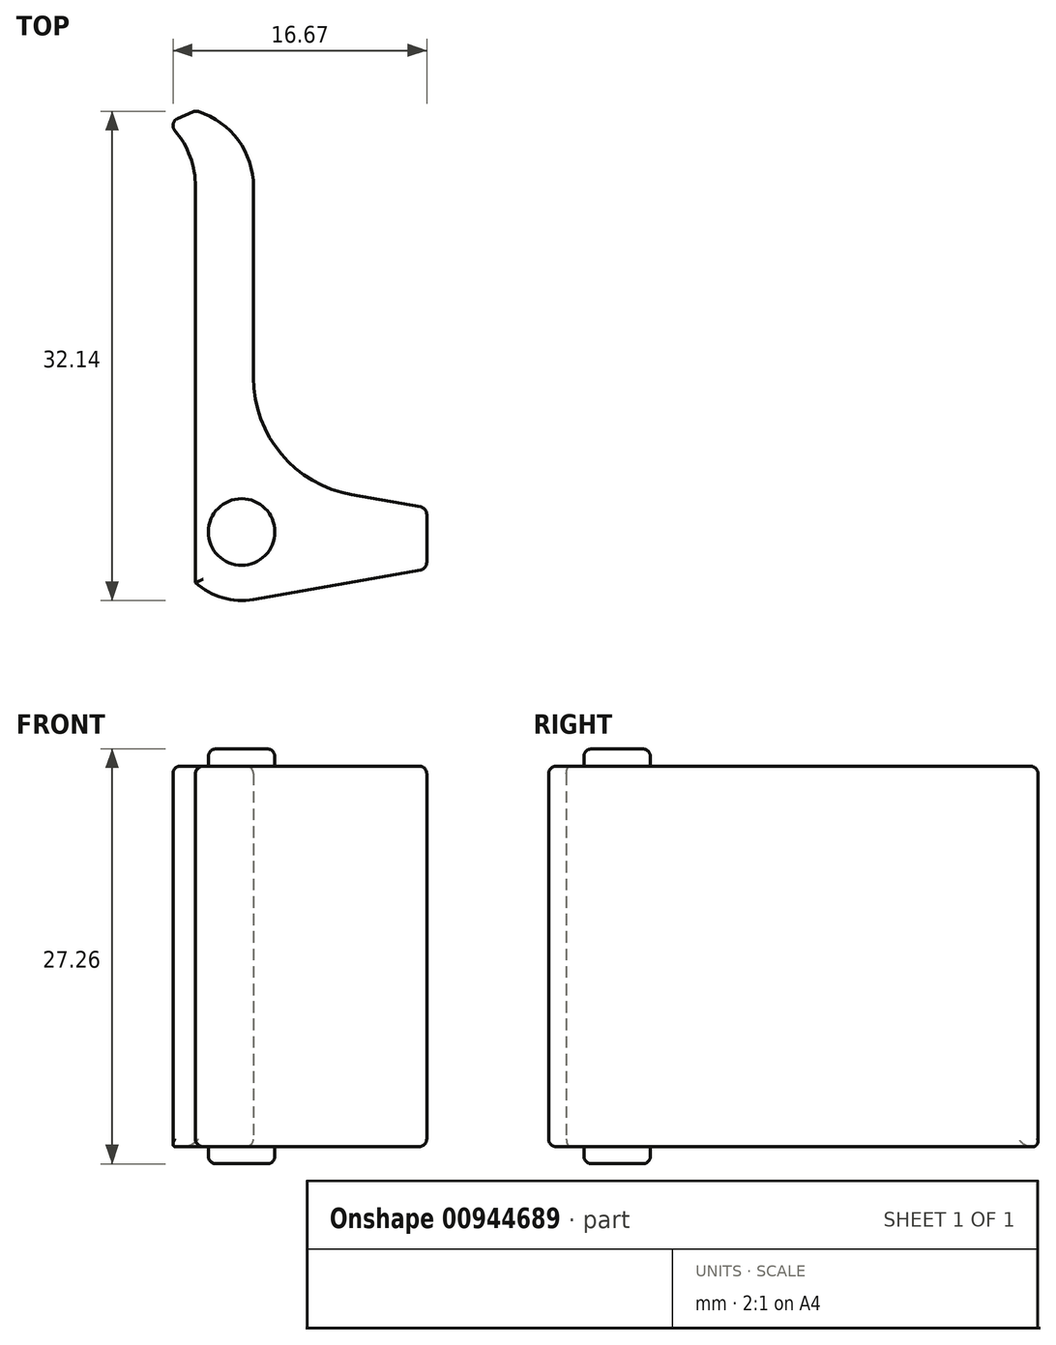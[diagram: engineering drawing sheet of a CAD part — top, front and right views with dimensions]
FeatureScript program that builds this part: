
annotation { "Feature Type Name" : "Feature", "Feature Type Description" : "" }
export const myFeature = defineFeature(function(context is Context, id is Id, definition is map)
    precondition{}
    {
        {
            var Q0;
            Q0=qCreatedBy(makeId("Top.planeOp"),FACE);
            var sketch = newSketch(context, id + "F0", { "sketchPlane" : qUnion([Q0])});
            skLineSegment(sketch, "E0", {"start": v(0, 0) * mm, "end": v(0, 26) * mm});
            skLineSegment(sketch, "E1", {"start": v(3.8, 26) * mm, "end": v(3.8, 13.46) * mm});
            skArc(sketch, "E2", {"start": v(3.8, 13.46) * mm, "mid": v(5.64, 8.44) * mm, "end": v(10.26, 5.77) * mm});
            skLineSegment(sketch, "E3", {"start": v(10.26, 5.77) * mm, "end": v(15.19, 4.9) * mm});
            skLineSegment(sketch, "E4", {"start": v(15.19, 4.9) * mm, "end": v(15.19, 0.9) * mm});
            skLineSegment(sketch, "E5", {"start": v(15.19, 0.9) * mm, "end": v(3.8, -1.1) * mm});
            skArc(sketch, "E6", {"start": v(0, 0) * mm, "mid": v(1.78, -1) * mm, "end": v(3.8, -1.1) * mm});
            skLineSegment(sketch, "E7", {"start": v(0, 26) * mm, "end": v(52.42, 26) * mm, "construction": true});
            skCircle(sketch, "E8", {"center": v(3.03, 3.33) * mm, "radius": 2.19 * mm});
            skPoint(sketch, "E9", {"position": v(15.19, 2.9) * mm});
            skPoint(sketch, "E10", {"position": v(1.14, 31.66) * mm});
            skLineSegment(sketch, "E11", {"start": v(1.14, 31.66) * mm, "end": v(15.19, 2.9) * mm, "construction": true});
            skLineSegment(sketch, "E12", {"start": v(3.03, 3.33) * mm, "end": v(3.03, -1.17) * mm, "construction": true});
            skArc(sketch, "E13", {"start": v(3.8, 26) * mm, "mid": v(2.75, 29.14) * mm, "end": v(0, 31) * mm});
            skLineSegment(sketch, "E14", {"start": v(1.14, 31.66) * mm, "end": v(-9.06, 26.67) * mm, "construction": true});
            skLineSegment(sketch, "E15", {"start": v(0, 31) * mm, "end": v(-1.83, 30.2) * mm});
            skArc(sketch, "E16", {"start": v(0, 26) * mm, "mid": v(-0.48, 28.3) * mm, "end": v(-1.83, 30.2) * mm});
            skSolve(sketch);
        }
        {
            var Q0;
            Q0=makeQuery(id+"F2.opExtrude","CAP_FACE",FACE,{"disambiguationData":[OSD([sQuery(id+"F0.wireOp",EDGE,"E0"),sQuery(id+"F0.wireOp",EDGE,"E1"),sQuery(id+"F0.wireOp",EDGE,"E2"),sQuery(id+"F0.wireOp",EDGE,"E3"),sQuery(id+"F0.wireOp",EDGE,"E4"),sQuery(id+"F0.wireOp",EDGE,"E5"),sQuery(id+"F0.wireOp",EDGE,"E6"),sQuery(id+"F0.wireOp",EDGE,"E13"),sQuery(id+"F0.wireOp",EDGE,"E15"),sQuery(id+"F0.wireOp",EDGE,"E16")])],"isStart":false});
            var Q1;
            Q1=makeQuery(id+"F0.imprint","IMPRINT",FACE,{"disambiguationData":[TD([[makeQuery(id+"F0.imprint","IMPRINT",EDGE,{"derivedFrom":sQuery(id+"F0.wireOp",EDGE,"E8")}),1.0]])]});
            extrude(context, id + "F1", {"entities" : qUnion([Q0, Q1]), "endBound" : BoundingType.SYMMETRIC, "depth" : 27.25 * mm, "offsetDistance" : 25 * mm});
        }
        {
            var Q0;
            Q0 = qSketchRegion(id + "F0", true);
            extrude(context, id + "F2", {"entities" : qUnion([Q0]), "operationType" : NewBodyOperationType.ADD, "endBound" : BoundingType.SYMMETRIC, "depth" : 25 * mm, "offsetDistance" : 25 * mm});
        }
        {
            var Q0;
            Q0=makeQuery(id+"F2.opExtrude","CAP_EDGE",EDGE,{"disambiguationData":[OSD([sQuery(id+"F0.wireOp",EDGE,"E6")])],"isStart":false});
            var Q1;
            Q1=makeQuery(id+"F2.opExtrude","CAP_EDGE",EDGE,{"disambiguationData":[OSD([sQuery(id+"F0.wireOp",EDGE,"E5")])],"isStart":false});
            var Q2;
            Q2=makeQuery(id+"F2.opExtrude","CAP_EDGE",EDGE,{"disambiguationData":[OSD([sQuery(id+"F0.wireOp",EDGE,"E0")])],"isStart":false});
            var Q3;
            Q3=makeQuery(id+"F2.opExtrude","CAP_EDGE",EDGE,{"disambiguationData":[OSD([sQuery(id+"F0.wireOp",EDGE,"E16")])],"isStart":false});
            var Q4;
            Q4=makeQuery(id+"F2.opExtrude","SWEPT_EDGE",EDGE,{"disambiguationData":[OSD([sQuery(id+"F0.wireOp",EDGE,"E15"),sQuery(id+"F0.wireOp",EDGE,"E16")])]});
            var Q5;
            Q5=makeQuery(id+"F2.opExtrude","SWEPT_EDGE",EDGE,{"disambiguationData":[OSD([sQuery(id+"F0.wireOp",EDGE,"E13"),sQuery(id+"F0.wireOp",EDGE,"E15")])]});
            var Q6;
            Q6=makeQuery(id+"F2.opExtrude","CAP_EDGE",EDGE,{"disambiguationData":[OSD([sQuery(id+"F0.wireOp",EDGE,"E0")])],"isStart":true});
            var Q7;
            Q7=makeQuery(id+"F2.opExtrude","CAP_EDGE",EDGE,{"disambiguationData":[OSD([sQuery(id+"F0.wireOp",EDGE,"E16")])],"isStart":true});
            var Q8;
            Q8=makeQuery(id+"F2.opExtrude","CAP_EDGE",EDGE,{"disambiguationData":[OSD([sQuery(id+"F0.wireOp",EDGE,"E13")])],"isStart":true});
            var Q9;
            Q9=makeQuery(id+"F2.opExtrude","CAP_EDGE",EDGE,{"disambiguationData":[OSD([sQuery(id+"F0.wireOp",EDGE,"E1")])],"isStart":true});
            var Q10;
            Q10=makeQuery(id+"F2.opExtrude","CAP_EDGE",EDGE,{"disambiguationData":[OSD([sQuery(id+"F0.wireOp",EDGE,"E2")])],"isStart":true});
            var Q11;
            Q11=makeQuery(id+"F2.opExtrude","CAP_EDGE",EDGE,{"disambiguationData":[OSD([sQuery(id+"F0.wireOp",EDGE,"E3")])],"isStart":true});
            var Q12;
            Q12=makeQuery(id+"F2.opExtrude","CAP_EDGE",EDGE,{"disambiguationData":[OSD([sQuery(id+"F0.wireOp",EDGE,"E4")])],"isStart":true});
            var Q13;
            Q13=makeQuery(id+"F2.opExtrude","CAP_EDGE",EDGE,{"disambiguationData":[OSD([sQuery(id+"F0.wireOp",EDGE,"E5")])],"isStart":true});
            var Q14;
            Q14=makeQuery(id+"F2.opExtrude","CAP_EDGE",EDGE,{"disambiguationData":[OSD([sQuery(id+"F0.wireOp",EDGE,"E6")])],"isStart":true});
            var Q15;
            Q15=makeQuery(id+"F2.opExtrude","SWEPT_EDGE",EDGE,{"disambiguationData":[OSD([sQuery(id+"F0.wireOp",EDGE,"E4"),sQuery(id+"F0.wireOp",EDGE,"E5")])]});
            var Q16;
            Q16=makeQuery(id+"F2.opExtrude","SWEPT_EDGE",EDGE,{"disambiguationData":[OSD([sQuery(id+"F0.wireOp",EDGE,"E3"),sQuery(id+"F0.wireOp",EDGE,"E4")])]});
            var Q17;
            Q17=makeQuery(id+"F2.opExtrude","CAP_EDGE",EDGE,{"disambiguationData":[OSD([sQuery(id+"F0.wireOp",EDGE,"E4")])],"isStart":false});
            var Q18;
            Q18=makeQuery(id+"F2.opExtrude","CAP_EDGE",EDGE,{"disambiguationData":[OSD([sQuery(id+"F0.wireOp",EDGE,"E3")])],"isStart":false});
            var Q19;
            Q19=makeQuery(id+"F2.opExtrude","CAP_EDGE",EDGE,{"disambiguationData":[OSD([sQuery(id+"F0.wireOp",EDGE,"E2")])],"isStart":false});
            var Q20;
            Q20=makeQuery(id+"F2.opExtrude","CAP_EDGE",EDGE,{"disambiguationData":[OSD([sQuery(id+"F0.wireOp",EDGE,"E1")])],"isStart":false});
            var Q21;
            Q21=makeQuery(id+"F2.opExtrude","CAP_EDGE",EDGE,{"disambiguationData":[OSD([sQuery(id+"F0.wireOp",EDGE,"E13")])],"isStart":false});
            var Q22;
            Q22=makeQuery(id+"F2.opExtrude","CAP_EDGE",EDGE,{"disambiguationData":[OSD([sQuery(id+"F0.wireOp",EDGE,"E15")])],"isStart":false});
            fillet(context, id + "F3", {"entities" : qUnion([Q0, Q1, Q2, Q3, Q4, Q5, Q6, Q7, Q8, Q9, Q10, Q11, Q12, Q13, Q14, Q15, Q16, Q17, Q18, Q19, Q20, Q21, Q22]), "radius" : .5 * mm, "tangentPropagation" : true, "allowEdgeOverflow" : false});
        }
        {
            var Q0;
            Q0=makeQuery(id+"F1.opExtrude","CAP_EDGE",EDGE,{"disambiguationData":[OSD([sQuery(id+"F0.wireOp",EDGE,"E8")])],"isStart":false});
            var Q1;
            Q1=makeQuery(id+"F1.opExtrude","CAP_EDGE",EDGE,{"disambiguationData":[OSD([sQuery(id+"F0.wireOp",EDGE,"E8")])],"isStart":true});
            fillet(context, id + "F4", {"entities" : qUnion([Q0, Q1]), "radius" : .5 * mm, "tangentPropagation" : true, "allowEdgeOverflow" : false});
        }
    });
